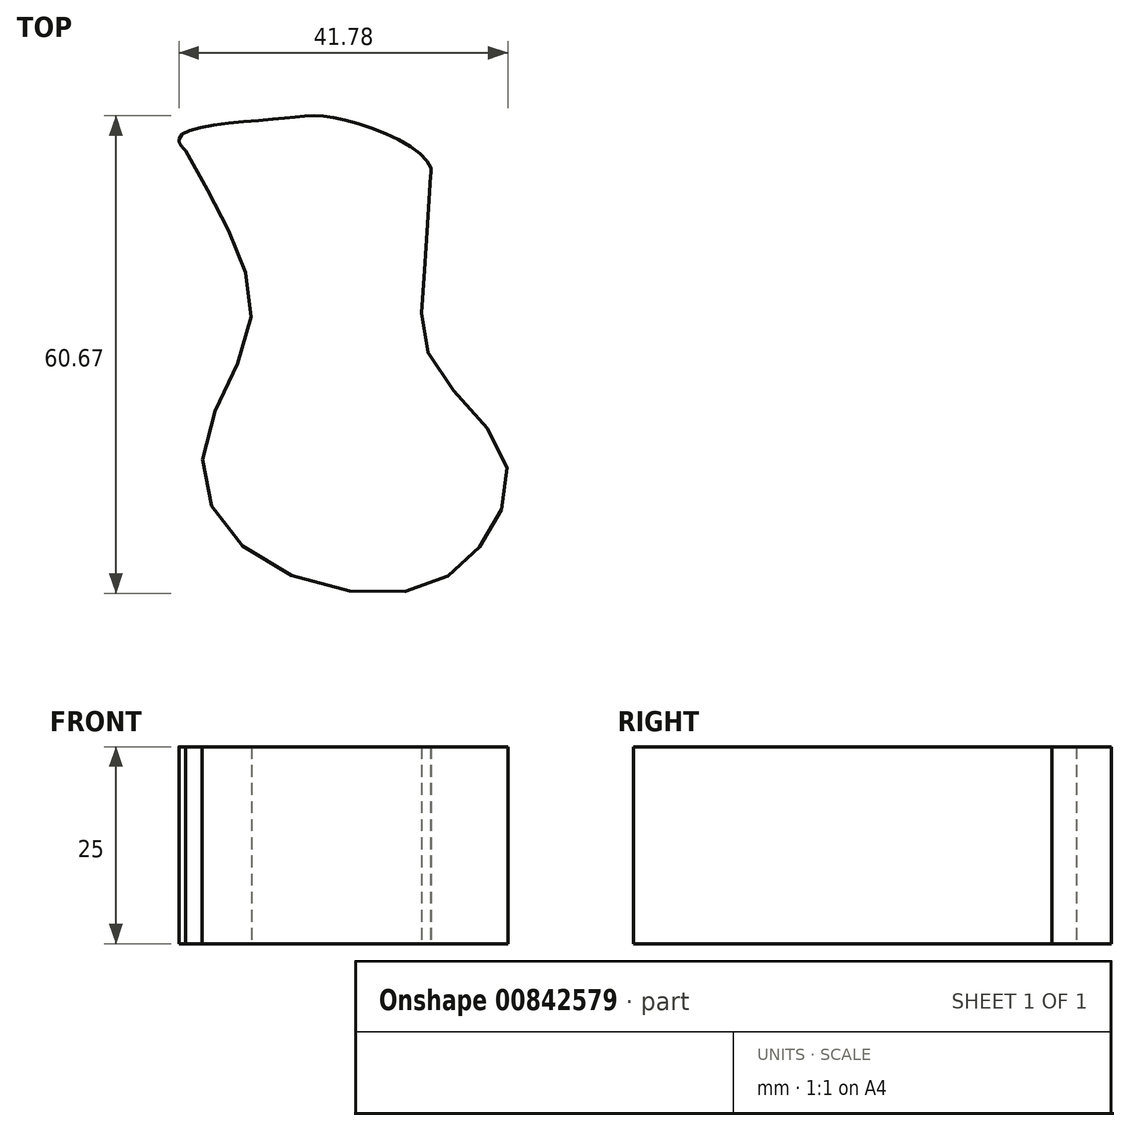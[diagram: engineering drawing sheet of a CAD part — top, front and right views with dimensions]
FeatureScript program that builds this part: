
annotation { "Feature Type Name" : "Feature", "Feature Type Description" : "" }
export const myFeature = defineFeature(function(context is Context, id is Id, definition is map)
    precondition{}
    {
        {
            var Q0;
            Q0=qCreatedBy(makeId("Top.planeOp"),FACE);
            var sketch = newSketch(context, id + "F0", { "sketchPlane" : qUnion([Q0])});
            skFitSpline(sketch, "E0", {"points": [v(-35.26, 23.92) * mm, v(-14.45, 15.84) * mm, v(-3.26, 20.2) * mm, v(-14.45, 26.4) * mm, v(-23.45, 26.4) * mm, v(-35.26, 23.92) * mm]});
            skFitSpline(sketch, "E1", {"points": [v(-35.26, 23.92) * mm, v(-29.05, 12.43) * mm, v(-26.25, 0) * mm, v(-32.15, -15.53) * mm, v(-26.25, -28.58) * mm, v(-6.37, -33.55) * mm, v(3.57, -27.03) * mm, v(6.06, -16.46) * mm, v(-2.95, -4.66) * mm, v(-4.2, 5.9) * mm, v(-3.26, 20.2) * mm], "startDerivative": vector(66.15, -116.12) * mm, "endDerivative": vector(8.65, 145.5) * mm});
            skSolve(sketch);
        }
        {
            var Q0;
            Q0 = qSketchRegion(id + "F0", true);
            extrude(context, id + "F1", {"entities" : qUnion([Q0]), "depth" : 25 * mm, "offsetDistance" : 25 * mm});
        }
    });
